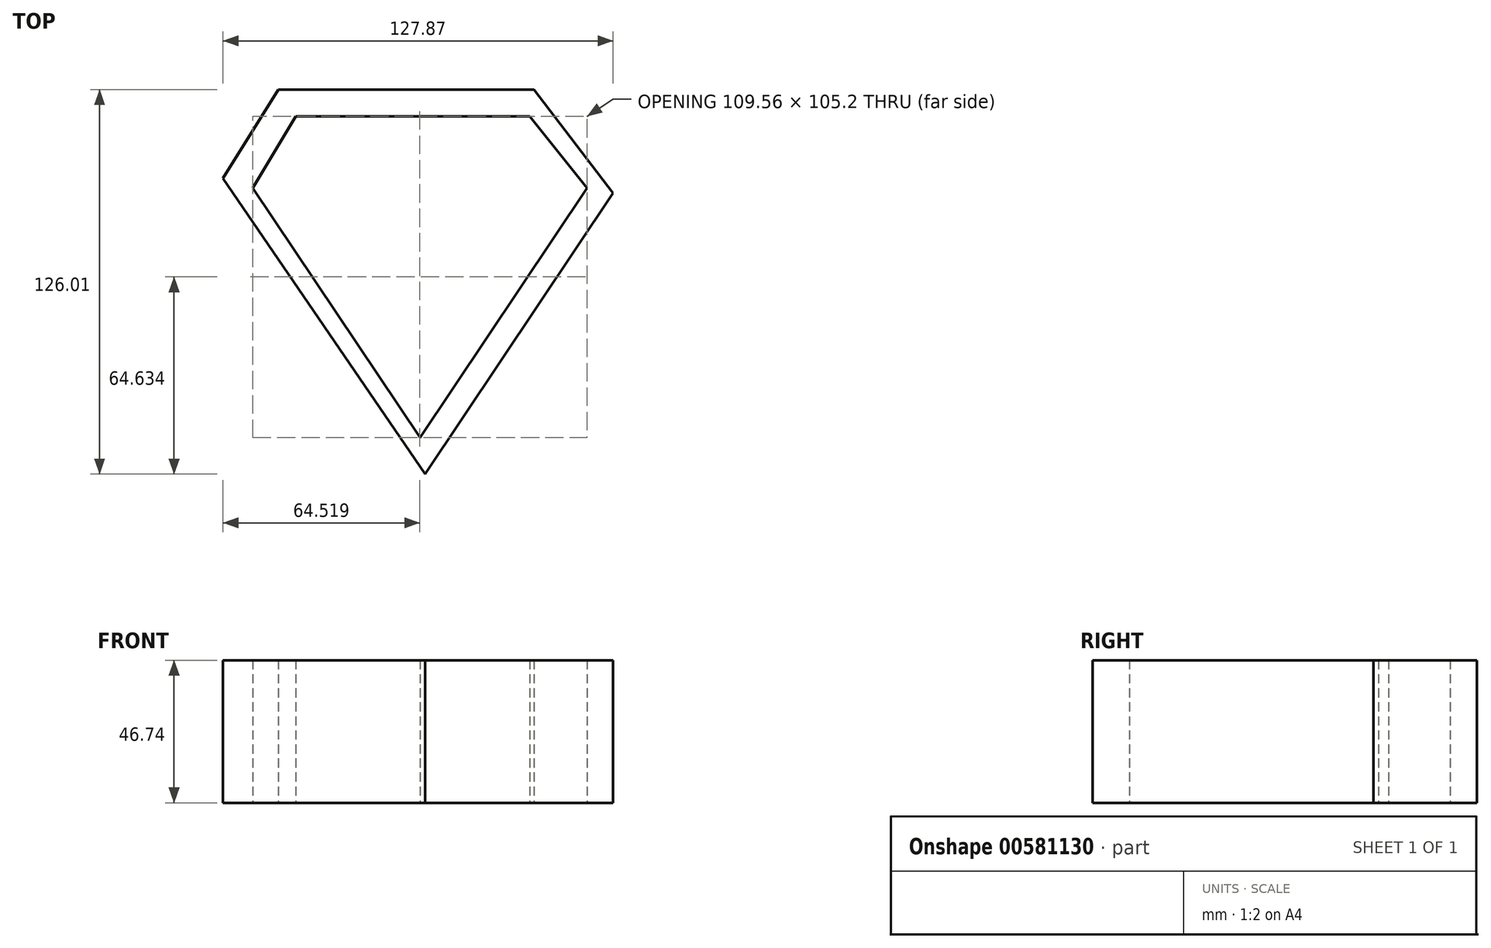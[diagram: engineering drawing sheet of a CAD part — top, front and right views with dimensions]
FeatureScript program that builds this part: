
annotation { "Feature Type Name" : "Feature", "Feature Type Description" : "" }
export const myFeature = defineFeature(function(context is Context, id is Id, definition is map)
    precondition{}
    {
        {
            var Q0;
            Q0=qCreatedBy(makeId("Top.planeOp"),FACE);
            var sketch = newSketch(context, id + "F0", { "sketchPlane" : qUnion([Q0])});
            skLineSegment(sketch, "E0", {"start": v(-40.86, 38.13) * mm, "end": v(35.89, 38.13) * mm});
            skLineSegment(sketch, "E1", {"start": v(35.89, 38.13) * mm, "end": v(54.65, 14.62) * mm});
            skLineSegment(sketch, "E2", {"start": v(-40.86, 38.13) * mm, "end": v(-54.91, 14.62) * mm});
            skLineSegment(sketch, "E3", {"start": v(-54.91, 14.62) * mm, "end": v(0, -67.06) * mm});
            skLineSegment(sketch, "E4", {"start": v(54.65, 14.62) * mm, "end": v(0, -67.06) * mm});
            skLineSegment(sketch, "E5", {"start": v(-46.47, 46.9) * mm, "end": v(37.3, 46.9) * mm});
            skLineSegment(sketch, "E6", {"start": v(37.3, 46.9) * mm, "end": v(63.22, 13.01) * mm});
            skLineSegment(sketch, "E7", {"start": v(63.22, 13.01) * mm, "end": v(1.6, -79.1) * mm});
            skLineSegment(sketch, "E8", {"start": v(1.6, -79.1) * mm, "end": v(-64.65, 17.84) * mm});
            skLineSegment(sketch, "E9", {"start": v(-64.65, 17.84) * mm, "end": v(-46.47, 46.9) * mm});
            skSolve(sketch);
        }
        {
            var Q0;
            Q0 = qSketchRegion(id + "F0", true);
            extrude(context, id + "F1", {"entities" : qUnion([Q0]), "depth" : 46.74 * mm, "offsetDistance" : 25.4 * mm});
        }
    });
